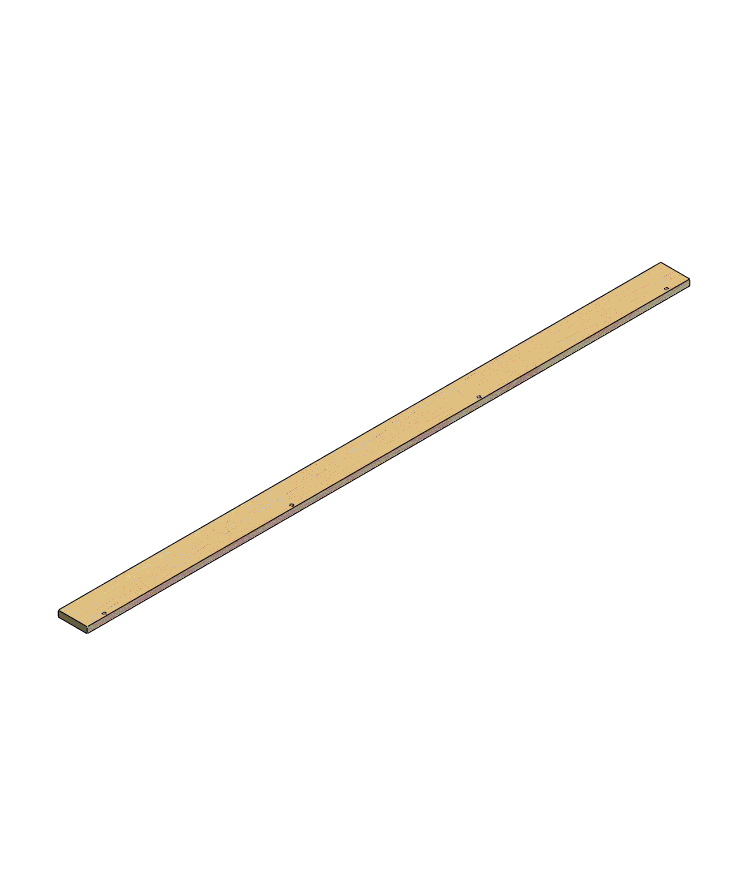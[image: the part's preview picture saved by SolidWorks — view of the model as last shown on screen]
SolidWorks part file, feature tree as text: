
SOLIDWORKS PART (.sldprt)
format: sldprt  version: not decoded by parser v0  size: 182,784 bytes
history: native  units: mm
features: sketch x3, cut_extrude x2, material x1, extrude x1 (+11 scaffold rows collapsed)
feature tree (18):
  scaffold x11  (default folders/planes/origin — collapsed)
  material  "Material <not specified>"
  sketch  "Sketch1"  dims[D1=1200.0mm D2=62.0mm]
  extrude  "Boss-Extrude1"  Depth=12mm
  sketch  "Sketch2"  dims[c1.D1=6.0mm c1.D2=6.0mm c1.D3=6.0mm c2.D2=6.0mm c2.D3=40.0mm c2.D5=40.0mm c2.D4=4.0]
  cut_extrude  "Cut-Extrude1"  Depth=22mm
  sketch  "Sketch3"  dims[D1=4.5mm D2=1524.0mm]
  cut_extrude  "Cut-Extrude2"  Depth=20mm
decode coverage: 6 of 6 modeling features carry decoded parameters
note: suppression state not decoded; provenance and decode notes live in map.json
